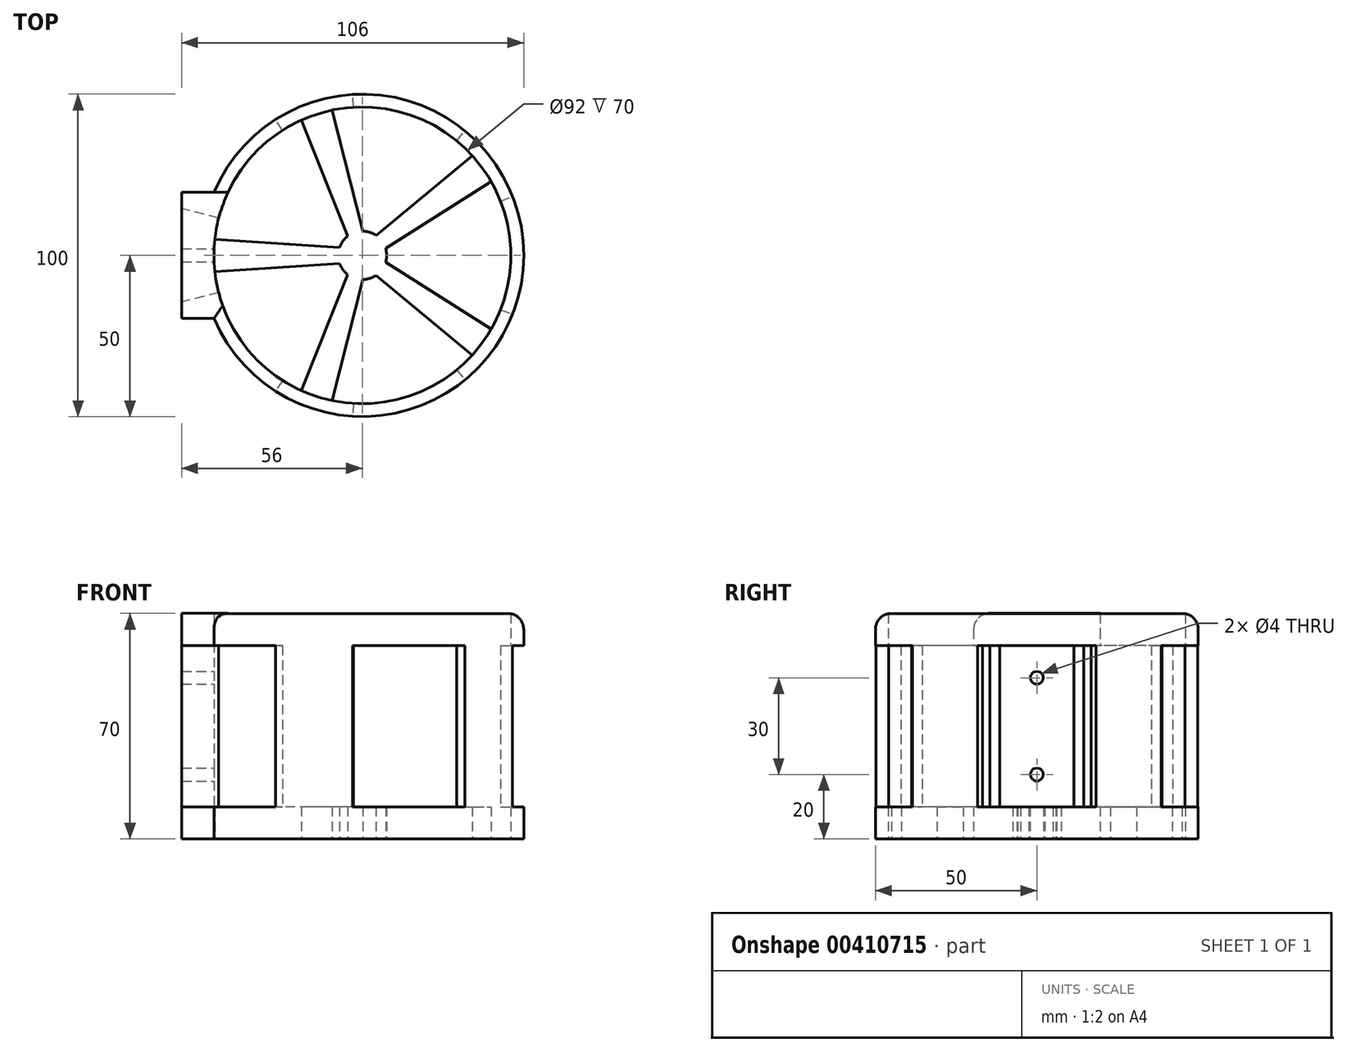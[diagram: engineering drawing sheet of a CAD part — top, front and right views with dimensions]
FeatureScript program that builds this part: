
annotation { "Feature Type Name" : "Feature", "Feature Type Description" : "" }
export const myFeature = defineFeature(function(context is Context, id is Id, definition is map)
    precondition{}
    {
        {
            var Q0;
            Q0=qCreatedBy(makeId("Top.planeOp"),FACE);
            var sketch = newSketch(context, id + "F0", { "sketchPlane" : qUnion([Q0])});
            skArc(sketch, "E0", {"start": v(-46, -19.6) * mm, "mid": v(50, 0) * mm, "end": v(-46, 19.6) * mm});
            skLineSegment(sketch, "E1", {"start": v(-46, -19.6) * mm, "end": v(-46, 19.6) * mm, "construction": true});
            skLineSegment(sketch, "E2", {"start": v(-46, 19.6) * mm, "end": v(-56, 19.6) * mm});
            skLineSegment(sketch, "E3", {"start": v(-46, -19.6) * mm, "end": v(-56, -19.6) * mm});
            skLineSegment(sketch, "E4", {"start": v(-56, -19.6) * mm, "end": v(-56, 19.6) * mm});
            skCircle(sketch, "E5", {"center": v(0, 0) * mm, "radius": 46 * mm});
            skSolve(sketch);
        }
        {
            var Q0;
            Q0=qSketchRegion(id+"F0",true);
            extrude(context, id + "F1", {"entities" : qUnion([Q0]), "depth" : 70 * mm});
        }
        {
            var Q0;
            Q0=makeQuery(id+"F1.opExtrude","CAP_FACE",FACE,{"disambiguationData":[OSD([sQuery(id+"F0.wireOp",EDGE,"E0"),sQuery(id+"F0.wireOp",EDGE,"E2"),sQuery(id+"F0.wireOp",EDGE,"E3"),sQuery(id+"F0.wireOp",EDGE,"E4"),sQuery(id+"F0.wireOp",EDGE,"E5")])],"isStart":true});
            var sketch = newSketch(context, id + "F2", { "sketchPlane" : qUnion([Q0])});
            skPoint(sketch, "E6", {"position": v(0, 0) * mm});
            skCircle(sketch, "E7", {"center": v(0, 0) * mm, "radius": 7.5 * mm});
            skLineSegment(sketch, "E8", {"start": v(-4.56, 5.95) * mm, "end": v(-18.89, 41.94) * mm});
            skLineSegment(sketch, "E9", {"start": v(0.2, 7.5) * mm, "end": v(-9.38, 45.03) * mm});
            skLineSegment(sketch, "E10", {"start": v(-18.89, 41.94) * mm, "end": v(-9.38, 45.03) * mm, "construction": true});
            skLineSegment(sketch, "E11", {"start": v(-4.56, 5.95) * mm, "end": v(0.2, 7.5) * mm, "construction": true});
            skLineSegment(sketch, "E12.1.0", {"start": v(-7.07, -2.5) * mm, "end": v(-45.73, -5) * mm});
            skLineSegment(sketch, "E12.1.1", {"start": v(-7.07, 2.5) * mm, "end": v(-45.73, 5) * mm});
            skLineSegment(sketch, "E12.1.2", {"start": v(-45.73, -5) * mm, "end": v(-45.73, 5) * mm, "construction": true});
            skLineSegment(sketch, "E12.1.3", {"start": v(-7.07, -2.5) * mm, "end": v(-7.07, 2.5) * mm, "construction": true});
            skLineSegment(sketch, "E12.2.0", {"start": v(0.2, -7.5) * mm, "end": v(-9.38, -45.03) * mm});
            skLineSegment(sketch, "E12.2.1", {"start": v(-4.56, -5.95) * mm, "end": v(-18.89, -41.94) * mm});
            skLineSegment(sketch, "E12.2.2", {"start": v(-9.38, -45.03) * mm, "end": v(-18.89, -41.94) * mm, "construction": true});
            skLineSegment(sketch, "E12.2.3", {"start": v(0.2, -7.5) * mm, "end": v(-4.56, -5.95) * mm, "construction": true});
            skLineSegment(sketch, "E13.1.3.0", {"start": v(7.2, -2.13) * mm, "end": v(39.93, -22.83) * mm});
            skLineSegment(sketch, "E13.3.3.0", {"start": v(4.25, -6.18) * mm, "end": v(34.06, -30.92) * mm});
            skLineSegment(sketch, "E13.6.3.0", {"start": v(39.93, -22.83) * mm, "end": v(34.06, -30.92) * mm, "construction": true});
            skLineSegment(sketch, "E13.9.3.0", {"start": v(7.2, -2.13) * mm, "end": v(4.25, -6.18) * mm, "construction": true});
            skLineSegment(sketch, "E13.1.4.0", {"start": v(4.25, 6.18) * mm, "end": v(34.06, 30.92) * mm});
            skLineSegment(sketch, "E13.3.4.0", {"start": v(7.2, 2.13) * mm, "end": v(39.93, 22.83) * mm});
            skLineSegment(sketch, "E13.6.4.0", {"start": v(34.06, 30.92) * mm, "end": v(39.93, 22.83) * mm, "construction": true});
            skLineSegment(sketch, "E13.9.4.0", {"start": v(4.25, 6.18) * mm, "end": v(7.2, 2.13) * mm, "construction": true});
            skSolve(sketch);
        }
        {
            var Q0;
            Q0=qSketchRegion(id+"F2",true);
            var Q1;
            {var subQ0=sQuery(id+"F2.wireOp",EDGE,"E12.1.0");Q1=makeQuery(id+"F2.imprint","IMPRINT",FACE,{"disambiguationData":[TD([[makeQuery(id+"F2.imprint","IMPRINT",EDGE,{"derivedFrom":subQ0}),-1.0]])]});}
            var Q2;
            {var subQ0=sQuery(id+"F2.wireOp",EDGE,"E8");Q2=makeQuery(id+"F2.imprint","IMPRINT",FACE,{"disambiguationData":[TD([[makeQuery(id+"F2.imprint","IMPRINT",EDGE,{"derivedFrom":subQ0}),-1.0]])]});}
            var Q3;
            {var subQ0=sQuery(id+"F2.wireOp",EDGE,"E13.1.4.0");Q3=makeQuery(id+"F2.imprint","IMPRINT",FACE,{"disambiguationData":[TD([[makeQuery(id+"F2.imprint","IMPRINT",EDGE,{"derivedFrom":subQ0}),-1.0]])]});}
            var Q4;
            {var subQ0=sQuery(id+"F2.wireOp",EDGE,"E13.1.3.0");Q4=makeQuery(id+"F2.imprint","IMPRINT",FACE,{"disambiguationData":[TD([[makeQuery(id+"F2.imprint","IMPRINT",EDGE,{"derivedFrom":subQ0}),-1.0]])]});}
            var Q5;
            {var subQ0=sQuery(id+"F2.wireOp",EDGE,"E12.2.0");Q5=makeQuery(id+"F2.imprint","IMPRINT",FACE,{"disambiguationData":[TD([[makeQuery(id+"F2.imprint","IMPRINT",EDGE,{"derivedFrom":subQ0}),-1.0]])]});}
            extrude(context, id + "F3", {"entities" : qUnion([Q0, Q1, Q2, Q3, Q4, Q5]), "operationType" : NewBodyOperationType.ADD, "oppositeDirection" : true, "depth" : 10 * mm});
        }
        {
            var Q0;
            Q0=makeQuery(id+"F3.opExtrude","CAP_FACE",FACE,{"disambiguationData":[OSD([sQuery(id+"F0.wireOp",EDGE,"E5"),sQuery(id+"F2.wireOp",EDGE,"E7"),sQuery(id+"F2.wireOp",EDGE,"E8"),sQuery(id+"F2.wireOp",EDGE,"E9"),sQuery(id+"F2.wireOp",EDGE,"E12.1.0"),sQuery(id+"F2.wireOp",EDGE,"E12.1.1"),sQuery(id+"F2.wireOp",EDGE,"E12.2.0"),sQuery(id+"F2.wireOp",EDGE,"E12.2.1"),sQuery(id+"F2.wireOp",EDGE,"E13.1.3.0"),sQuery(id+"F2.wireOp",EDGE,"E13.3.3.0"),sQuery(id+"F2.wireOp",EDGE,"E13.1.4.0"),sQuery(id+"F2.wireOp",EDGE,"E13.3.4.0")])],"isStart":false});
            cPlane(context, id + "F4", {"entities" : qUnion([Q0]), "cplaneType" : CPlaneType.OFFSET, "offset" : 0 * mm, "width" : 150 * mm, "height" : 150 * mm});
        }
        {
            var Q0;
            Q0=qCreatedBy(id+"F4.planeOp",FACE);
            var sketch = newSketch(context, id + "F5", { "sketchPlane" : qUnion([Q0])});
            skCircle(sketch, "E14", {"center": v(0, 0) * mm, "radius": 76.53 * mm, "construction": true});
            skCircle(sketch, "E15", {"center": v(0, 0) * mm, "radius": 46 * mm, "construction": true});
            skArc(sketch, "E16", {"start": v(42.8, -16.84) * mm, "mid": v(46, 0) * mm, "end": v(42.8, 16.84) * mm});
            skLineSegment(sketch, "E17", {"start": v(42.8, -16.84) * mm, "end": v(42.8, 16.84) * mm});
            skArc(sketch, "E18", {"start": v(71.22, -28) * mm, "mid": v(76.53, 0) * mm, "end": v(71.22, 28) * mm});
            skLineSegment(sketch, "E19", {"start": v(42.8, -16.84) * mm, "end": v(71.22, -28) * mm});
            skLineSegment(sketch, "E20", {"start": v(42.8, 16.84) * mm, "end": v(71.22, 28) * mm});
            skLineSegment(sketch, "E21", {"start": v(42.8, -16.84) * mm, "end": v(0, 0) * mm, "construction": true});
            skLineSegment(sketch, "E22", {"start": v(42.8, 16.84) * mm, "end": v(0, 0) * mm, "construction": true});
            skLineSegment(sketch, "E23.1.0", {"start": v(29.24, 35.51) * mm, "end": v(48.65, 59.08) * mm});
            skLineSegment(sketch, "E23.1.1", {"start": v(-2.78, 45.92) * mm, "end": v(-4.63, 76.39) * mm});
            skLineSegment(sketch, "E23.1.2", {"start": v(29.24, 35.51) * mm, "end": v(-2.78, 45.92) * mm});
            skArc(sketch, "E23.1.3", {"start": v(48.65, 59.08) * mm, "mid": v(23.65, 72.78) * mm, "end": v(-4.63, 76.39) * mm});
            skLineSegment(sketch, "E23.2.0", {"start": v(-24.74, 38.78) * mm, "end": v(-41.15, 64.52) * mm});
            skLineSegment(sketch, "E23.2.1", {"start": v(-44.53, 11.54) * mm, "end": v(-74.08, 19.2) * mm});
            skLineSegment(sketch, "E23.2.2", {"start": v(-24.74, 38.78) * mm, "end": v(-44.53, 11.54) * mm});
            skArc(sketch, "E23.2.3", {"start": v(-41.15, 64.52) * mm, "mid": v(-61.91, 44.98) * mm, "end": v(-74.08, 19.2) * mm});
            skLineSegment(sketch, "E24.1.3.0", {"start": v(-44.53, -11.54) * mm, "end": v(-74.08, -19.2) * mm});
            skLineSegment(sketch, "E24.3.3.0", {"start": v(-24.74, -38.78) * mm, "end": v(-41.15, -64.52) * mm});
            skLineSegment(sketch, "E24.6.3.0", {"start": v(-44.53, -11.54) * mm, "end": v(-24.74, -38.78) * mm});
            skArc(sketch, "E24.9.3.0", {"start": v(-74.08, -19.2) * mm, "mid": v(-61.91, -44.98) * mm, "end": v(-41.15, -64.52) * mm});
            skLineSegment(sketch, "E24.1.4.0", {"start": v(-2.78, -45.92) * mm, "end": v(-4.63, -76.39) * mm});
            skLineSegment(sketch, "E24.3.4.0", {"start": v(29.24, -35.51) * mm, "end": v(48.65, -59.08) * mm});
            skLineSegment(sketch, "E24.6.4.0", {"start": v(-2.78, -45.92) * mm, "end": v(29.24, -35.51) * mm});
            skArc(sketch, "E24.9.4.0", {"start": v(-4.63, -76.39) * mm, "mid": v(23.65, -72.78) * mm, "end": v(48.65, -59.08) * mm});
            skSolve(sketch);
        }
        {
            var Q0;
            Q0=qSketchRegion(id+"F5",true);
            extrude(context, id + "F6", {"entities" : qUnion([Q0]), "operationType" : NewBodyOperationType.REMOVE, "depth" : 50 * mm});
        }
        {
            var Q0;
            Q0=qCreatedBy(makeId("Right.planeOp"),FACE);
            var sketch = newSketch(context, id + "F7", { "sketchPlane" : qUnion([Q0])});
            skLineSegment(sketch, "E25", {"start": v(0, 0) * mm, "end": v(0, 42.9) * mm, "construction": true});
            skPoint(sketch, "E26", {"position": v(0, 21.45) * mm});
            skCircle(sketch, "E27", {"center": v(0, 50) * mm, "radius": 2 * mm});
            skCircle(sketch, "E28", {"center": v(0, 20) * mm, "radius": 2 * mm});
            skSolve(sketch);
        }
        {
            var Q0;
            Q0=qSketchRegion(id+"F7",true);
            extrude(context, id + "F8", {"entities" : qUnion([Q0]), "operationType" : NewBodyOperationType.REMOVE, "endBound" : BoundingType.THROUGH_ALL, "oppositeDirection" : true, "depth" : 25 * mm});
        }
        {
            var Q0;
            Q0=makeQuery(id+"F1.opExtrude","CAP_EDGE",EDGE,{"disambiguationData":[OSD([sQuery(id+"F0.wireOp",EDGE,"E0")])],"isStart":false});
            fillet(context, id + "F9", {"entities" : qUnion([Q0]), "radius" : 5 * mm, "tangentPropagation" : true, "allowEdgeOverflow" : false});
        }
        {
            var Q0;
            Q0=makeQuery(id+"F1.opExtrude","CAP_EDGE",EDGE,{"disambiguationData":[OSD([sQuery(id+"F0.wireOp",EDGE,"E3")])],"isStart":false});
            fillet(context, id + "F10", {"entities" : qUnion([Q0]), "radius" : 5 * mm, "tangentPropagation" : true, "allowEdgeOverflow" : false});
        }
    });
